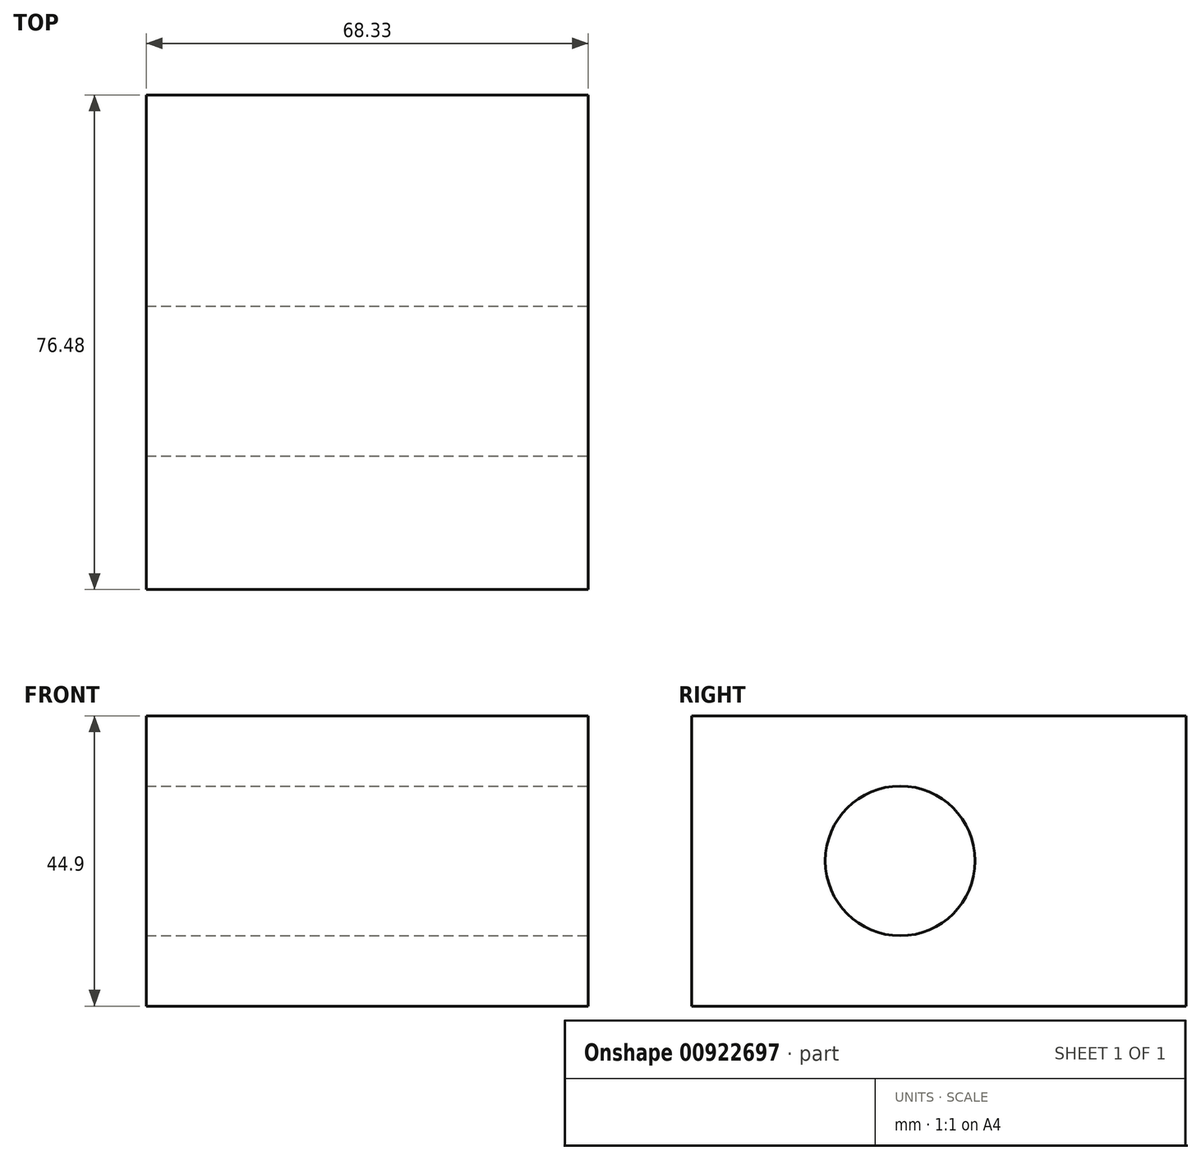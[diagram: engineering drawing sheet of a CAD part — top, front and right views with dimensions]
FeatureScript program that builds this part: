
annotation { "Feature Type Name" : "Feature", "Feature Type Description" : "" }
export const myFeature = defineFeature(function(context is Context, id is Id, definition is map)
    precondition{}
    {
        {
            var Q0;
            Q0=qCreatedBy(makeId("Right.planeOp"),FACE);
            var sketch = newSketch(context, id + "F0", { "sketchPlane" : qUnion([Q0])});
            skLineSegment(sketch, "E0.bottom", {"start": v(-47.03, 51.42) * mm, "end": v(29.45, 51.42) * mm});
            skLineSegment(sketch, "E0.top", {"start": v(-47.03, 6.52) * mm, "end": v(29.45, 6.52) * mm});
            skLineSegment(sketch, "E0.left", {"start": v(-47.03, 51.42) * mm, "end": v(-47.03, 6.52) * mm});
            skLineSegment(sketch, "E0.right", {"start": v(29.45, 51.42) * mm, "end": v(29.45, 6.52) * mm});
            skSolve(sketch);
        }
        {
            var Q0;
            Q0=makeQuery(id+"F0.imprint","IMPRINT",FACE,{"disambiguationData":[TD([[makeQuery(id+"F0.imprint","IMPRINT",EDGE,{"derivedFrom":sQuery(id+"F0.wireOp",EDGE,"E0.bottom")}),-1.0]])]});
            extrude(context, id + "F1", {"entities" : qUnion([Q0]), "depth" : 68.33 * mm, "offsetDistance" : 25.4 * mm});
        }
        {
            var Q0;
            Q0=makeQuery(id+"F1.opExtrude","CAP_FACE",FACE,{"disambiguationData":[OSD([sQuery(id+"F0.wireOp",EDGE,"E0.bottom"),sQuery(id+"F0.wireOp",EDGE,"E0.top"),sQuery(id+"F0.wireOp",EDGE,"E0.left"),sQuery(id+"F0.wireOp",EDGE,"E0.right")])],"isStart":false});
            var sketch = newSketch(context, id + "F2", { "sketchPlane" : qUnion([Q0])});
            skCircle(sketch, "E1", {"center": v(-14.79, 28.97) * mm, "radius": 11.58 * mm});
            skPoint(sketch, "E1.centerSnap0", {"position": v(29.45, 28.97) * mm});
            skSolve(sketch);
        }
        {
            var Q0;
            Q0=makeQuery(id+"F2.imprint","IMPRINT",FACE,{"disambiguationData":[TD([[makeQuery(id+"F2.imprint","IMPRINT",EDGE,{"derivedFrom":sQuery(id+"F2.wireOp",EDGE,"E1")}),1.0]])]});
            extrude(context, id + "F3", {"entities" : qUnion([Q0]), "operationType" : NewBodyOperationType.REMOVE, "oppositeDirection" : true, "depth" : 188.72 * mm, "offsetDistance" : 25.4 * mm});
        }
    });
